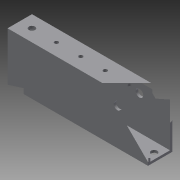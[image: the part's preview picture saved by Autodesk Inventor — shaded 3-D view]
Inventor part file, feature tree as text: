
AUTODESK INVENTOR PART (.ipt)
format: ipt  version: 2015 SP1 (Build 190203100, 203)  size: 140,800 bytes
history: native  units: in
note: dims shown in document units (in); Inventor stores cm internally (conversion verified against a paired STEP export)
features: sketch x5, projected_geometry x4, hole x3, extrude x2, pattern_linear x1
ambient origin geometry x8: Origin, YZ Plane, XZ Plane, XY Plane, X Axis, Y Axis, Z Axis, Center Point
bodies: Solid1 (feature_tree)
feature tree (15):
  extrude  "Extrusion1"  Depth=1.0in
  hole  "Hole3"  [1 undecoded]
  pattern_linear  "Rectangular Pattern1"  Spacing1=0.5in  [1 undecoded]
  hole  "Hole4"  [1 undecoded]
  extrude  "Extrusion3"  Depth=1.0in
  hole  "Hole5"  [1 undecoded]
  sketch  "Sketch1"  dims[d0=2.0in d1=1.0in]
  sketch  "Sketch5"  dims[d2=1.8in d3=0.8in]
  projected_geometry  "Projected Loop4"
  sketch  "Sketch6"  dims[d4=0.1in]
  projected_geometry  "Projected Loop5"
  sketch  "Sketch7"  dims[d5=0.1in]
  projected_geometry  "Projected Loop6"
  sketch  "Sketch8"  dims[d6=5.75in d7=0.0in d39=0.5in d40=0.5in d41=0.1562in d42=0.75in d43=0.375in d44=0.25in d45=0.5635in d46=1.0in d47=0.8108in d48=2.3622in d50=1.0in d51=0.5in d52=1.25in d53=0.3125in d54=0.75in d55=0.375in d56=0.25in d57=0.5635in d58=1.0in d59=0.8108in d60=0.25in d61=0.25in d62=2.0in d63=0.0in d64=0.75in d65=1.0in d66=0.3125in d67=0.75in d68=0.375in d69=0.25in d70=0.5635in d71=1.0in d72=0.8108in]
  projected_geometry  "Projected Loop7"
note: 4 required parameter values undecoded (feature->parameter linkage not recoverable at this tier; creation-order binding heuristic only, values carry confidence <= 0.55)
